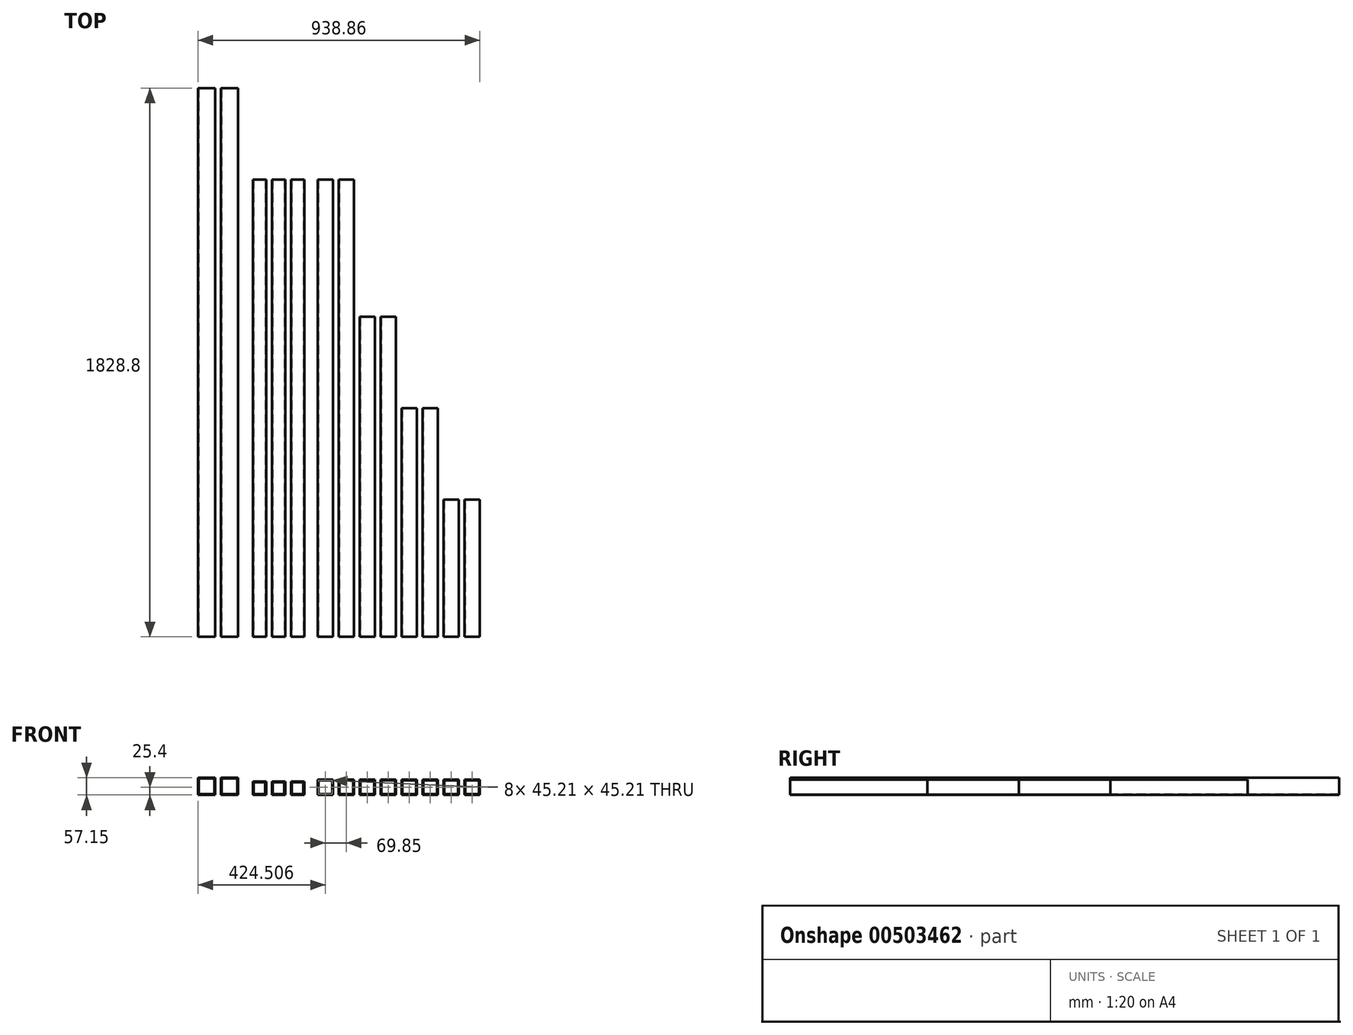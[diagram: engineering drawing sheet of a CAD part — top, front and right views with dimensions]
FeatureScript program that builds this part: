
annotation { "Feature Type Name" : "Feature", "Feature Type Description" : "" }
export const myFeature = defineFeature(function(context is Context, id is Id, definition is map)
    precondition{}
    {
        {
            var Q0;
            Q0=qCreatedBy(makeId("Front.planeOp"),FACE);
            var sketch = newSketch(context, id + "F0", { "sketchPlane" : qUnion([Q0])});
            skLineSegment(sketch, "E0.bottom", {"start": v(-53.27, 0) * mm, "end": v(-2.47, 0) * mm});
            skLineSegment(sketch, "E0.top", {"start": v(-53.27, 50.8) * mm, "end": v(-2.47, 50.8) * mm});
            skLineSegment(sketch, "E0.left", {"start": v(-53.27, 0) * mm, "end": v(-53.27, 50.8) * mm});
            skLineSegment(sketch, "E0.right", {"start": v(-2.47, 0) * mm, "end": v(-2.47, 50.8) * mm});
            skLineSegment(sketch, "E1.bottom", {"start": v(-5.27, 48) * mm, "end": v(-50.48, 48) * mm});
            skLineSegment(sketch, "E1.top", {"start": v(-5.27, 2.8) * mm, "end": v(-50.48, 2.8) * mm});
            skLineSegment(sketch, "E1.left", {"start": v(-5.27, 48) * mm, "end": v(-5.27, 2.8) * mm});
            skLineSegment(sketch, "E1.right", {"start": v(-50.48, 48) * mm, "end": v(-50.48, 2.8) * mm});
            skLineSegment(sketch, "E2.bottom", {"start": v(-269.68, 0) * mm, "end": v(-225.23, 0) * mm});
            skLineSegment(sketch, "E2.top", {"start": v(-269.68, 44.45) * mm, "end": v(-225.23, 44.45) * mm});
            skLineSegment(sketch, "E2.left", {"start": v(-269.68, 0) * mm, "end": v(-269.68, 44.45) * mm});
            skLineSegment(sketch, "E2.right", {"start": v(-225.23, 0) * mm, "end": v(-225.23, 44.45) * mm});
            skLineSegment(sketch, "E3.bottom", {"start": v(-228.03, 41.66) * mm, "end": v(-266.89, 41.66) * mm});
            skLineSegment(sketch, "E3.top", {"start": v(-228.03, 2.8) * mm, "end": v(-266.89, 2.8) * mm});
            skLineSegment(sketch, "E3.left", {"start": v(-228.03, 41.66) * mm, "end": v(-228.03, 2.8) * mm});
            skLineSegment(sketch, "E3.right", {"start": v(-266.89, 41.66) * mm, "end": v(-266.89, 2.8) * mm});
            skLineSegment(sketch, "E4.bottom", {"start": v(-452.38, 0) * mm, "end": v(-395.23, 0) * mm});
            skLineSegment(sketch, "E4.top", {"start": v(-452.38, 57.15) * mm, "end": v(-395.23, 57.15) * mm});
            skLineSegment(sketch, "E4.left", {"start": v(-452.38, 0) * mm, "end": v(-452.38, 57.15) * mm});
            skLineSegment(sketch, "E4.right", {"start": v(-395.23, 0) * mm, "end": v(-395.23, 57.15) * mm});
            skLineSegment(sketch, "E5.bottom", {"start": v(-398.03, 54.36) * mm, "end": v(-449.59, 54.36) * mm});
            skLineSegment(sketch, "E5.top", {"start": v(-398.03, 2.8) * mm, "end": v(-449.59, 2.8) * mm});
            skLineSegment(sketch, "E5.left", {"start": v(-398.03, 54.36) * mm, "end": v(-398.03, 2.8) * mm});
            skLineSegment(sketch, "E5.right", {"start": v(-449.59, 54.36) * mm, "end": v(-449.59, 2.8) * mm});
            skLineSegment(sketch, "E6.1.0.0", {"start": v(16.58, 0) * mm, "end": v(67.38, 0) * mm});
            skLineSegment(sketch, "E6.1.0.1", {"start": v(64.58, 48) * mm, "end": v(64.58, 2.8) * mm});
            skLineSegment(sketch, "E6.1.0.2", {"start": v(19.37, 48) * mm, "end": v(19.37, 2.8) * mm});
            skLineSegment(sketch, "E6.1.0.3", {"start": v(67.38, 0) * mm, "end": v(67.38, 50.8) * mm});
            skLineSegment(sketch, "E6.1.0.4", {"start": v(64.58, 48) * mm, "end": v(19.37, 48) * mm});
            skLineSegment(sketch, "E6.1.0.5", {"start": v(64.58, 2.8) * mm, "end": v(19.37, 2.8) * mm});
            skLineSegment(sketch, "E6.1.0.6", {"start": v(16.58, 50.8) * mm, "end": v(67.38, 50.8) * mm});
            skLineSegment(sketch, "E6.1.0.7", {"start": v(16.58, 0) * mm, "end": v(16.58, 50.8) * mm});
            skLineSegment(sketch, "E6.2.0.0", {"start": v(86.43, 0) * mm, "end": v(137.23, 0) * mm});
            skLineSegment(sketch, "E6.2.0.1", {"start": v(134.43, 48) * mm, "end": v(134.43, 2.8) * mm});
            skLineSegment(sketch, "E6.2.0.2", {"start": v(89.22, 48) * mm, "end": v(89.22, 2.8) * mm});
            skLineSegment(sketch, "E6.2.0.3", {"start": v(137.23, 0) * mm, "end": v(137.23, 50.8) * mm});
            skLineSegment(sketch, "E6.2.0.4", {"start": v(134.43, 48) * mm, "end": v(89.22, 48) * mm});
            skLineSegment(sketch, "E6.2.0.5", {"start": v(134.43, 2.8) * mm, "end": v(89.22, 2.8) * mm});
            skLineSegment(sketch, "E6.2.0.6", {"start": v(86.43, 50.8) * mm, "end": v(137.23, 50.8) * mm});
            skLineSegment(sketch, "E6.2.0.7", {"start": v(86.43, 0) * mm, "end": v(86.43, 50.8) * mm});
            skLineSegment(sketch, "E6.3.0.0", {"start": v(156.28, 0) * mm, "end": v(207.08, 0) * mm});
            skLineSegment(sketch, "E6.3.0.1", {"start": v(204.28, 48) * mm, "end": v(204.28, 2.8) * mm});
            skLineSegment(sketch, "E6.3.0.2", {"start": v(159.07, 48) * mm, "end": v(159.07, 2.8) * mm});
            skLineSegment(sketch, "E6.3.0.3", {"start": v(207.08, 0) * mm, "end": v(207.08, 50.8) * mm});
            skLineSegment(sketch, "E6.3.0.4", {"start": v(204.28, 48) * mm, "end": v(159.07, 48) * mm});
            skLineSegment(sketch, "E6.3.0.5", {"start": v(204.28, 2.8) * mm, "end": v(159.07, 2.8) * mm});
            skLineSegment(sketch, "E6.3.0.6", {"start": v(156.28, 50.8) * mm, "end": v(207.08, 50.8) * mm});
            skLineSegment(sketch, "E6.3.0.7", {"start": v(156.28, 0) * mm, "end": v(156.28, 50.8) * mm});
            skLineSegment(sketch, "E6.4.0.0", {"start": v(226.13, 0) * mm, "end": v(276.93, 0) * mm});
            skLineSegment(sketch, "E6.4.0.1", {"start": v(274.13, 48) * mm, "end": v(274.13, 2.8) * mm});
            skLineSegment(sketch, "E6.4.0.2", {"start": v(228.92, 48) * mm, "end": v(228.92, 2.8) * mm});
            skLineSegment(sketch, "E6.4.0.3", {"start": v(276.93, 0) * mm, "end": v(276.93, 50.8) * mm});
            skLineSegment(sketch, "E6.4.0.4", {"start": v(274.13, 48) * mm, "end": v(228.92, 48) * mm});
            skLineSegment(sketch, "E6.4.0.5", {"start": v(274.13, 2.8) * mm, "end": v(228.92, 2.8) * mm});
            skLineSegment(sketch, "E6.4.0.6", {"start": v(226.13, 50.8) * mm, "end": v(276.93, 50.8) * mm});
            skLineSegment(sketch, "E6.4.0.7", {"start": v(226.13, 0) * mm, "end": v(226.13, 50.8) * mm});
            skLineSegment(sketch, "E6.5.0.0", {"start": v(295.98, 0) * mm, "end": v(346.78, 0) * mm});
            skLineSegment(sketch, "E6.5.0.1", {"start": v(343.98, 48) * mm, "end": v(343.98, 2.8) * mm});
            skLineSegment(sketch, "E6.5.0.2", {"start": v(298.77, 48) * mm, "end": v(298.77, 2.8) * mm});
            skLineSegment(sketch, "E6.5.0.3", {"start": v(346.78, 0) * mm, "end": v(346.78, 50.8) * mm});
            skLineSegment(sketch, "E6.5.0.4", {"start": v(343.98, 48) * mm, "end": v(298.77, 48) * mm});
            skLineSegment(sketch, "E6.5.0.5", {"start": v(343.98, 2.8) * mm, "end": v(298.77, 2.8) * mm});
            skLineSegment(sketch, "E6.5.0.6", {"start": v(295.98, 50.8) * mm, "end": v(346.78, 50.8) * mm});
            skLineSegment(sketch, "E6.5.0.7", {"start": v(295.98, 0) * mm, "end": v(295.98, 50.8) * mm});
            skLineSegment(sketch, "E6.6.0.0", {"start": v(365.83, 0) * mm, "end": v(416.63, 0) * mm});
            skLineSegment(sketch, "E6.6.0.1", {"start": v(413.83, 48) * mm, "end": v(413.83, 2.8) * mm});
            skLineSegment(sketch, "E6.6.0.2", {"start": v(368.62, 48) * mm, "end": v(368.62, 2.8) * mm});
            skLineSegment(sketch, "E6.6.0.3", {"start": v(416.63, 0) * mm, "end": v(416.63, 50.8) * mm});
            skLineSegment(sketch, "E6.6.0.4", {"start": v(413.83, 48) * mm, "end": v(368.62, 48) * mm});
            skLineSegment(sketch, "E6.6.0.5", {"start": v(413.83, 2.8) * mm, "end": v(368.62, 2.8) * mm});
            skLineSegment(sketch, "E6.6.0.6", {"start": v(365.83, 50.8) * mm, "end": v(416.63, 50.8) * mm});
            skLineSegment(sketch, "E6.6.0.7", {"start": v(365.83, 0) * mm, "end": v(365.83, 50.8) * mm});
            skLineSegment(sketch, "E6.7.0.0", {"start": v(435.68, 0) * mm, "end": v(486.48, 0) * mm});
            skLineSegment(sketch, "E6.7.0.1", {"start": v(483.68, 48) * mm, "end": v(483.68, 2.8) * mm});
            skLineSegment(sketch, "E6.7.0.2", {"start": v(438.47, 48) * mm, "end": v(438.47, 2.8) * mm});
            skLineSegment(sketch, "E6.7.0.3", {"start": v(486.48, 0) * mm, "end": v(486.48, 50.8) * mm});
            skLineSegment(sketch, "E6.7.0.4", {"start": v(483.68, 48) * mm, "end": v(438.47, 48) * mm});
            skLineSegment(sketch, "E6.7.0.5", {"start": v(483.68, 2.8) * mm, "end": v(438.47, 2.8) * mm});
            skLineSegment(sketch, "E6.7.0.6", {"start": v(435.68, 50.8) * mm, "end": v(486.48, 50.8) * mm});
            skLineSegment(sketch, "E6.7.0.7", {"start": v(435.68, 0) * mm, "end": v(435.68, 50.8) * mm});
            skLineSegment(sketch, "E6.direction1", {"start": v(-53.27, 0) * mm, "end": v(16.58, 0) * mm, "construction": true});
            skLineSegment(sketch, "E7.1.0.0", {"start": v(-206.18, 44.45) * mm, "end": v(-161.73, 44.45) * mm});
            skLineSegment(sketch, "E7.1.0.1", {"start": v(-206.18, 0) * mm, "end": v(-206.18, 44.45) * mm});
            skLineSegment(sketch, "E7.1.0.2", {"start": v(-164.53, 41.66) * mm, "end": v(-164.53, 2.8) * mm});
            skLineSegment(sketch, "E7.1.0.3", {"start": v(-164.53, 41.66) * mm, "end": v(-203.39, 41.66) * mm});
            skLineSegment(sketch, "E7.1.0.4", {"start": v(-161.73, 0) * mm, "end": v(-161.73, 44.45) * mm});
            skLineSegment(sketch, "E7.1.0.5", {"start": v(-164.53, 2.8) * mm, "end": v(-203.39, 2.8) * mm});
            skLineSegment(sketch, "E7.1.0.6", {"start": v(-203.39, 41.66) * mm, "end": v(-203.39, 2.8) * mm});
            skLineSegment(sketch, "E7.1.0.7", {"start": v(-206.18, 0) * mm, "end": v(-161.73, 0) * mm});
            skLineSegment(sketch, "E7.2.0.0", {"start": v(-142.68, 44.45) * mm, "end": v(-98.23, 44.45) * mm});
            skLineSegment(sketch, "E7.2.0.1", {"start": v(-142.68, 0) * mm, "end": v(-142.68, 44.45) * mm});
            skLineSegment(sketch, "E7.2.0.2", {"start": v(-101.03, 41.66) * mm, "end": v(-101.03, 2.8) * mm});
            skLineSegment(sketch, "E7.2.0.3", {"start": v(-101.03, 41.66) * mm, "end": v(-139.89, 41.66) * mm});
            skLineSegment(sketch, "E7.2.0.4", {"start": v(-98.23, 0) * mm, "end": v(-98.23, 44.45) * mm});
            skLineSegment(sketch, "E7.2.0.5", {"start": v(-101.03, 2.8) * mm, "end": v(-139.89, 2.8) * mm});
            skLineSegment(sketch, "E7.2.0.6", {"start": v(-139.89, 41.66) * mm, "end": v(-139.89, 2.8) * mm});
            skLineSegment(sketch, "E7.2.0.7", {"start": v(-142.68, 0) * mm, "end": v(-98.23, 0) * mm});
            skLineSegment(sketch, "E7.direction1", {"start": v(-269.68, 0) * mm, "end": v(-206.18, 0) * mm, "construction": true});
            skLineSegment(sketch, "E8.1.0.0", {"start": v(-321.83, 2.8) * mm, "end": v(-373.39, 2.8) * mm});
            skLineSegment(sketch, "E8.1.0.1", {"start": v(-373.39, 54.36) * mm, "end": v(-373.39, 2.8) * mm});
            skLineSegment(sketch, "E8.1.0.2", {"start": v(-376.18, 0) * mm, "end": v(-319.03, 0) * mm});
            skLineSegment(sketch, "E8.1.0.3", {"start": v(-321.83, 54.36) * mm, "end": v(-373.39, 54.36) * mm});
            skLineSegment(sketch, "E8.1.0.4", {"start": v(-376.18, 57.15) * mm, "end": v(-319.03, 57.15) * mm});
            skLineSegment(sketch, "E8.1.0.5", {"start": v(-321.83, 54.36) * mm, "end": v(-321.83, 2.8) * mm});
            skLineSegment(sketch, "E8.1.0.6", {"start": v(-319.03, 0) * mm, "end": v(-319.03, 57.15) * mm});
            skLineSegment(sketch, "E8.1.0.7", {"start": v(-376.18, 0) * mm, "end": v(-376.18, 57.15) * mm});
            skLineSegment(sketch, "E8.direction1", {"start": v(-452.38, 0) * mm, "end": v(-376.18, 0) * mm, "construction": true});
            skSolve(sketch);
        }
        {
            var Q0;
            Q0=makeQuery(id+"F0.imprint","IMPRINT",FACE,{"disambiguationData":[TD([[makeQuery(id+"F0.imprint","IMPRINT",EDGE,{"derivedFrom":sQuery(id+"F0.wireOp",EDGE,"E2.bottom")}),1.0]])]});
            var Q1;
            Q1=makeQuery(id+"F0.imprint","IMPRINT",FACE,{"disambiguationData":[TD([[makeQuery(id+"F0.imprint","IMPRINT",EDGE,{"derivedFrom":sQuery(id+"F0.wireOp",EDGE,"E7.1.0.0")}),-1.0]])]});
            var Q2;
            Q2=makeQuery(id+"F0.imprint","IMPRINT",FACE,{"disambiguationData":[TD([[makeQuery(id+"F0.imprint","IMPRINT",EDGE,{"derivedFrom":sQuery(id+"F0.wireOp",EDGE,"E7.2.0.0")}),-1.0]])]});
            extrude(context, id + "F1", {"entities" : qUnion([Q0, Q1, Q2]), "oppositeDirection" : true, "depth" : 1524 * mm, "offsetDistance" : 25.4 * mm});
        }
        {
            var Q0;
            Q0=makeQuery(id+"F0.imprint","IMPRINT",FACE,{"disambiguationData":[TD([[makeQuery(id+"F0.imprint","IMPRINT",EDGE,{"derivedFrom":sQuery(id+"F0.wireOp",EDGE,"E0.bottom")}),1.0]])]});
            var Q1;
            Q1=makeQuery(id+"F0.imprint","IMPRINT",FACE,{"disambiguationData":[TD([[makeQuery(id+"F0.imprint","IMPRINT",EDGE,{"derivedFrom":sQuery(id+"F0.wireOp",EDGE,"E6.1.0.0")}),1.0]])]});
            extrude(context, id + "F2", {"entities" : qUnion([Q0, Q1]), "oppositeDirection" : true, "depth" : 1524 * mm, "offsetDistance" : 25.4 * mm});
        }
        {
            var Q0;
            Q0=makeQuery(id+"F0.imprint","IMPRINT",FACE,{"disambiguationData":[TD([[makeQuery(id+"F0.imprint","IMPRINT",EDGE,{"derivedFrom":sQuery(id+"F0.wireOp",EDGE,"E6.2.0.0")}),1.0]])]});
            var Q1;
            Q1=makeQuery(id+"F0.imprint","IMPRINT",FACE,{"disambiguationData":[TD([[makeQuery(id+"F0.imprint","IMPRINT",EDGE,{"derivedFrom":sQuery(id+"F0.wireOp",EDGE,"E6.3.0.0")}),1.0]])]});
            extrude(context, id + "F3", {"entities" : qUnion([Q0, Q1]), "oppositeDirection" : true, "depth" : 1066.8 * mm, "offsetDistance" : 25.4 * mm});
        }
        {
            var Q0;
            Q0=makeQuery(id+"F0.imprint","IMPRINT",FACE,{"disambiguationData":[TD([[makeQuery(id+"F0.imprint","IMPRINT",EDGE,{"derivedFrom":sQuery(id+"F0.wireOp",EDGE,"E6.4.0.0")}),1.0]])]});
            var Q1;
            Q1=makeQuery(id+"F0.imprint","IMPRINT",FACE,{"disambiguationData":[TD([[makeQuery(id+"F0.imprint","IMPRINT",EDGE,{"derivedFrom":sQuery(id+"F0.wireOp",EDGE,"E6.5.0.0")}),1.0]])]});
            extrude(context, id + "F4", {"entities" : qUnion([Q0, Q1]), "oppositeDirection" : true, "depth" : 762 * mm, "offsetDistance" : 25.4 * mm});
        }
        {
            var Q0;
            Q0=makeQuery(id+"F0.imprint","IMPRINT",FACE,{"disambiguationData":[TD([[makeQuery(id+"F0.imprint","IMPRINT",EDGE,{"derivedFrom":sQuery(id+"F0.wireOp",EDGE,"E6.6.0.0")}),1.0]])]});
            var Q1;
            Q1=makeQuery(id+"F0.imprint","IMPRINT",FACE,{"disambiguationData":[TD([[makeQuery(id+"F0.imprint","IMPRINT",EDGE,{"derivedFrom":sQuery(id+"F0.wireOp",EDGE,"E6.7.0.0")}),1.0]])]});
            extrude(context, id + "F5", {"entities" : qUnion([Q0, Q1]), "oppositeDirection" : true, "depth" : 457.2 * mm, "offsetDistance" : 25.4 * mm});
        }
        {
            var Q0;
            Q0=makeQuery(id+"F0.imprint","IMPRINT",FACE,{"disambiguationData":[TD([[makeQuery(id+"F0.imprint","IMPRINT",EDGE,{"derivedFrom":sQuery(id+"F0.wireOp",EDGE,"E4.bottom")}),1.0]])]});
            var Q1;
            Q1=makeQuery(id+"F0.imprint","IMPRINT",FACE,{"disambiguationData":[TD([[makeQuery(id+"F0.imprint","IMPRINT",EDGE,{"derivedFrom":sQuery(id+"F0.wireOp",EDGE,"E8.1.0.0")}),1.0]])]});
            extrude(context, id + "F6", {"entities" : qUnion([Q0, Q1]), "oppositeDirection" : true, "depth" : 1828.8 * mm, "offsetDistance" : 25.4 * mm});
        }
    });
